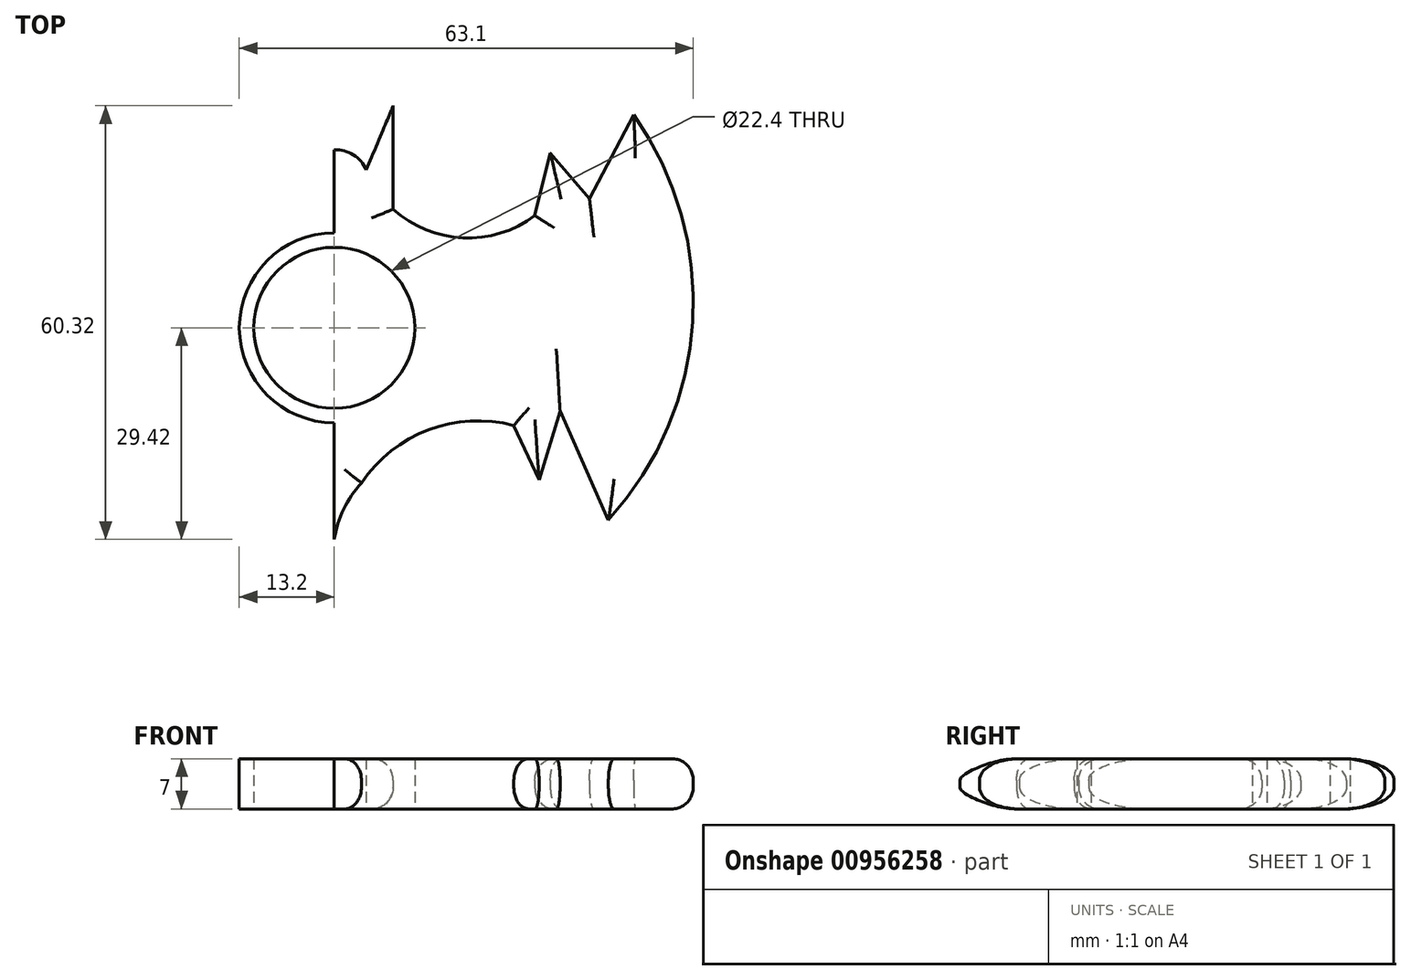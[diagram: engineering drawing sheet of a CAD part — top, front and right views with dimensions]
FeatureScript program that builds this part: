
annotation { "Feature Type Name" : "Feature", "Feature Type Description" : "" }
export const myFeature = defineFeature(function(context is Context, id is Id, definition is map)
    precondition{}
    {
        {
            var Q0;
            Q0=qCreatedBy(makeId("Top.planeOp"),FACE);
            var sketch = newSketch(context, id + "F0", { "sketchPlane" : qUnion([Q0])});
            skCircle(sketch, "E0", {"center": v(0, 0) * mm, "radius": 11.2 * mm});
            skCircle(sketch, "E1", {"center": v(0, 0) * mm, "radius": 13.2 * mm});
            skArc(sketch, "E2", {"start": v(-38.1, 26.72) * mm, "mid": v(-49.82, -0.84) * mm, "end": v(-41.61, -29.64) * mm});
            skArc(sketch, "E3.1.0", {"start": v(38.1, -26.72) * mm, "mid": v(49.82, 0.84) * mm, "end": v(41.61, 29.64) * mm});
            skLineSegment(sketch, "E4", {"start": v(-41.61, -29.64) * mm, "end": v(-35.48, -17.96) * mm});
            skLineSegment(sketch, "E5", {"start": v(-35.48, -17.96) * mm, "end": v(-35.48, -24.97) * mm});
            skArc(sketch, "E6", {"start": v(-4.53, -22.63) * mm, "mid": v(-14.98, -15.03) * mm, "end": v(-27.89, -15.62) * mm});
            skLineSegment(sketch, "E7.1.0", {"start": v(41.61, 29.64) * mm, "end": v(35.48, 17.96) * mm});
            skLineSegment(sketch, "E7.1.1", {"start": v(35.48, 17.96) * mm, "end": v(30.03, 24.29) * mm});
            skLineSegment(sketch, "E7.1.2", {"start": v(30.03, 24.29) * mm, "end": v(27.89, 15.62) * mm});
            skLineSegment(sketch, "E8", {"start": v(38.1, -26.72) * mm, "end": v(31.4, -11.53) * mm});
            skLineSegment(sketch, "E9", {"start": v(31.4, -11.53) * mm, "end": v(28.47, -21.17) * mm});
            skLineSegment(sketch, "E10", {"start": v(28.47, -21.17) * mm, "end": v(24.97, -13.58) * mm});
            skArc(sketch, "E11.1.0", {"start": v(-24.97, 13.58) * mm, "mid": v(-15.85, 12.08) * mm, "end": v(-7.74, 16.5) * mm});
            skLineSegment(sketch, "E11.1.2", {"start": v(-28.47, 21.17) * mm, "end": v(-24.97, 13.58) * mm});
            skLineSegment(sketch, "E11.1.4", {"start": v(-31.4, 11.53) * mm, "end": v(-28.47, 21.17) * mm});
            skLineSegment(sketch, "E11.1.5", {"start": v(-38.1, 26.72) * mm, "end": v(-31.4, 11.53) * mm});
            skArc(sketch, "E12", {"start": v(0, -34.06) * mm, "mid": v(-0.76, -27.75) * mm, "end": v(-4.53, -22.63) * mm});
            skArc(sketch, "E13.1.0", {"start": v(8.2, 16.53) * mm, "mid": v(17.88, 12.52) * mm, "end": v(27.89, 15.62) * mm});
            skLineSegment(sketch, "E14", {"start": v(-7.74, 16.5) * mm, "end": v(-7.74, 29.75) * mm});
            skLineSegment(sketch, "E15", {"start": v(-7.74, 29.75) * mm, "end": v(-4.12, 21.97) * mm});
            skLineSegment(sketch, "E16", {"start": v(8.2, 16.53) * mm, "end": v(8.2, 30.9) * mm});
            skLineSegment(sketch, "E17", {"start": v(8.2, 30.9) * mm, "end": v(4.45, 21.97) * mm});
            skArc(sketch, "E18", {"start": v(4.45, 21.97) * mm, "mid": v(0.16, 24.78) * mm, "end": v(-4.12, 21.97) * mm});
            skArc(sketch, "E19", {"start": v(24.97, -13.58) * mm, "mid": v(13.1, -14.2) * mm, "end": v(3.78, -21.57) * mm});
            skArc(sketch, "E20", {"start": v(3.78, -21.57) * mm, "mid": v(0.47, -27.38) * mm, "end": v(0, -34.06) * mm});
            skLineSegment(sketch, "E21.1.0", {"start": v(-35.48, -17.96) * mm, "end": v(-30.03, -24.29) * mm});
            skLineSegment(sketch, "E21.1.1", {"start": v(-30.03, -24.29) * mm, "end": v(-27.89, -15.62) * mm});
            skLineSegment(sketch, "E22", {"start": v(0, 24.77) * mm, "end": v(0, -34.06) * mm});
            skSolve(sketch);
        }
        {
            var Q0;
            Q0=makeQuery(id+"F0.imprint","IMPRINT",FACE,{"disambiguationData":[TD([[makeQuery(id+"F0.imprint","IMPRINT",EDGE,{"derivedFrom":sQuery(id+"F0.wireOp",EDGE,"E0")}),-1.0]])]});
            var Q1;
            Q1=makeQuery(id+"F0.imprint","IMPRINT",FACE,{"disambiguationData":[TD([[makeQuery(id+"F0.imprint","IMPRINT",EDGE,{"derivedFrom":sQuery(id+"F0.wireOp",EDGE,"E1")}),-1.0]])]});
            extrude(context, id + "F1", {"entities" : qUnion([Q0, Q1]), "depth" : 7 * mm, "offsetDistance" : 25 * mm});
        }
        {
            var Q0;
            Q0=makeQuery(id+"F1.opExtrude","CAP_EDGE",EDGE,{"disambiguationData":[OSD([sQuery(id+"F0.wireOp",EDGE,"E20")])],"isStart":false});
            var Q1;
            Q1=makeQuery(id+"F1.opExtrude","CAP_EDGE",EDGE,{"disambiguationData":[OSD([sQuery(id+"F0.wireOp",EDGE,"E19")])],"isStart":false});
            var Q2;
            Q2=makeQuery(id+"F1.opExtrude","CAP_EDGE",EDGE,{"disambiguationData":[OSD([sQuery(id+"F0.wireOp",EDGE,"E9")])],"isStart":false});
            var Q3;
            Q3=makeQuery(id+"F1.opExtrude","CAP_EDGE",EDGE,{"disambiguationData":[OSD([sQuery(id+"F0.wireOp",EDGE,"E3.1.0")])],"isStart":false});
            var Q4;
            Q4=makeQuery(id+"F1.opExtrude","CAP_EDGE",EDGE,{"disambiguationData":[OSD([sQuery(id+"F0.wireOp",EDGE,"E8")])],"isStart":false});
            var Q5;
            Q5=makeQuery(id+"F1.opExtrude","CAP_EDGE",EDGE,{"disambiguationData":[OSD([sQuery(id+"F0.wireOp",EDGE,"E7.1.0")])],"isStart":false});
            var Q6;
            Q6=makeQuery(id+"F1.opExtrude","CAP_EDGE",EDGE,{"disambiguationData":[OSD([sQuery(id+"F0.wireOp",EDGE,"E7.1.1")])],"isStart":false});
            var Q7;
            Q7=makeQuery(id+"F1.opExtrude","CAP_EDGE",EDGE,{"disambiguationData":[OSD([sQuery(id+"F0.wireOp",EDGE,"E7.1.2")])],"isStart":false});
            var Q8;
            Q8=makeQuery(id+"F1.opExtrude","CAP_EDGE",EDGE,{"disambiguationData":[OSD([sQuery(id+"F0.wireOp",EDGE,"E13.1.0")])],"isStart":false});
            var Q9;
            Q9=makeQuery(id+"F1.opExtrude","CAP_EDGE",EDGE,{"disambiguationData":[OSD([sQuery(id+"F0.wireOp",EDGE,"E16")])],"isStart":false});
            var Q10;
            Q10=makeQuery(id+"F1.opExtrude","CAP_EDGE",EDGE,{"disambiguationData":[OSD([sQuery(id+"F0.wireOp",EDGE,"E14")])],"isStart":false});
            var Q11;
            Q11=makeQuery(id+"F1.opExtrude","CAP_EDGE",EDGE,{"disambiguationData":[OSD([sQuery(id+"F0.wireOp",EDGE,"E11.1.0")])],"isStart":false});
            var Q12;
            Q12=makeQuery(id+"F1.opExtrude","CAP_EDGE",EDGE,{"disambiguationData":[OSD([sQuery(id+"F0.wireOp",EDGE,"E11.1.2")])],"isStart":false});
            var Q13;
            Q13=makeQuery(id+"F1.opExtrude","CAP_EDGE",EDGE,{"disambiguationData":[OSD([sQuery(id+"F0.wireOp",EDGE,"E11.1.5")])],"isStart":false});
            var Q14;
            Q14=makeQuery(id+"F1.opExtrude","CAP_EDGE",EDGE,{"disambiguationData":[OSD([sQuery(id+"F0.wireOp",EDGE,"E11.1.4")])],"isStart":false});
            var Q15;
            Q15=makeQuery(id+"F1.opExtrude","CAP_EDGE",EDGE,{"disambiguationData":[OSD([sQuery(id+"F0.wireOp",EDGE,"E2")])],"isStart":false});
            var Q16;
            Q16=makeQuery(id+"F1.opExtrude","CAP_EDGE",EDGE,{"disambiguationData":[OSD([sQuery(id+"F0.wireOp",EDGE,"E4")])],"isStart":false});
            var Q17;
            Q17=makeQuery(id+"F1.opExtrude","CAP_EDGE",EDGE,{"disambiguationData":[OSD([sQuery(id+"F0.wireOp",EDGE,"wEF84jsq-XExs-cQrN-D3yr-Ib7uIkRzdJAm")])],"isStart":false});
            var Q18;
            Q18=makeQuery(id+"F1.opExtrude","CAP_EDGE",EDGE,{"disambiguationData":[OSD([sQuery(id+"F0.wireOp",EDGE,"E12")])],"isStart":false});
            var Q19;
            Q19=makeQuery(id+"F1.opExtrude","CAP_EDGE",EDGE,{"disambiguationData":[OSD([sQuery(id+"F0.wireOp",EDGE,"E5")])],"isStart":false});
            var Q20;
            Q20=makeQuery(id+"F1.opExtrude","CAP_EDGE",EDGE,{"disambiguationData":[OSD([sQuery(id+"F0.wireOp",EDGE,"E10")])],"isStart":false});
            var Q21;
            Q21=makeQuery(id+"F1.opExtrude","CAP_EDGE",EDGE,{"disambiguationData":[OSD([sQuery(id+"F0.wireOp",EDGE,"E21.1.1")])],"isStart":false});
            var Q22;
            Q22=makeQuery(id+"F1.opExtrude","CAP_EDGE",EDGE,{"disambiguationData":[OSD([sQuery(id+"F0.wireOp",EDGE,"E6")])],"isStart":false});
            var Q23;
            Q23=makeQuery(id+"F1.opExtrude","CAP_EDGE",EDGE,{"disambiguationData":[OSD([sQuery(id+"F0.wireOp",EDGE,"E21.1.0")])],"isStart":false});
            var Q24;
            Q24=makeQuery(id+"F1.opExtrude","CAP_EDGE",EDGE,{"disambiguationData":[OSD([sQuery(id+"F0.wireOp",EDGE,"E3.1.0")])],"isStart":true});
            var Q25;
            Q25=makeQuery(id+"F1.opExtrude","CAP_EDGE",EDGE,{"disambiguationData":[OSD([sQuery(id+"F0.wireOp",EDGE,"E8")])],"isStart":true});
            var Q26;
            Q26=makeQuery(id+"F1.opExtrude","CAP_EDGE",EDGE,{"disambiguationData":[OSD([sQuery(id+"F0.wireOp",EDGE,"E9")])],"isStart":true});
            var Q27;
            Q27=makeQuery(id+"F1.opExtrude","CAP_EDGE",EDGE,{"disambiguationData":[OSD([sQuery(id+"F0.wireOp",EDGE,"E10")])],"isStart":true});
            var Q28;
            Q28=makeQuery(id+"F1.opExtrude","CAP_EDGE",EDGE,{"disambiguationData":[OSD([sQuery(id+"F0.wireOp",EDGE,"E19")])],"isStart":true});
            var Q29;
            Q29=makeQuery(id+"F1.opExtrude","CAP_EDGE",EDGE,{"disambiguationData":[OSD([sQuery(id+"F0.wireOp",EDGE,"E6")])],"isStart":true});
            var Q30;
            Q30=makeQuery(id+"F1.opExtrude","CAP_EDGE",EDGE,{"disambiguationData":[OSD([sQuery(id+"F0.wireOp",EDGE,"E12")])],"isStart":true});
            var Q31;
            Q31=makeQuery(id+"F1.opExtrude","CAP_EDGE",EDGE,{"disambiguationData":[OSD([sQuery(id+"F0.wireOp",EDGE,"E20")])],"isStart":true});
            var Q32;
            Q32=makeQuery(id+"F1.opExtrude","CAP_EDGE",EDGE,{"disambiguationData":[OSD([sQuery(id+"F0.wireOp",EDGE,"E21.1.1")])],"isStart":true});
            var Q33;
            Q33=makeQuery(id+"F1.opExtrude","CAP_EDGE",EDGE,{"disambiguationData":[OSD([sQuery(id+"F0.wireOp",EDGE,"E21.1.0")])],"isStart":true});
            var Q34;
            Q34=makeQuery(id+"F1.opExtrude","CAP_EDGE",EDGE,{"disambiguationData":[OSD([sQuery(id+"F0.wireOp",EDGE,"E4")])],"isStart":true});
            var Q35;
            Q35=makeQuery(id+"F1.opExtrude","CAP_EDGE",EDGE,{"disambiguationData":[OSD([sQuery(id+"F0.wireOp",EDGE,"E2")])],"isStart":true});
            var Q36;
            Q36=makeQuery(id+"F1.opExtrude","CAP_EDGE",EDGE,{"disambiguationData":[OSD([sQuery(id+"F0.wireOp",EDGE,"E11.1.5")])],"isStart":true});
            var Q37;
            Q37=makeQuery(id+"F1.opExtrude","CAP_EDGE",EDGE,{"disambiguationData":[OSD([sQuery(id+"F0.wireOp",EDGE,"E11.1.4")])],"isStart":true});
            var Q38;
            Q38=makeQuery(id+"F1.opExtrude","CAP_EDGE",EDGE,{"disambiguationData":[OSD([sQuery(id+"F0.wireOp",EDGE,"E14")])],"isStart":true});
            var Q39;
            Q39=makeQuery(id+"F1.opExtrude","CAP_EDGE",EDGE,{"disambiguationData":[OSD([sQuery(id+"F0.wireOp",EDGE,"E16")])],"isStart":true});
            var Q40;
            Q40=makeQuery(id+"F1.opExtrude","CAP_EDGE",EDGE,{"disambiguationData":[OSD([sQuery(id+"F0.wireOp",EDGE,"E13.1.0")])],"isStart":true});
            var Q41;
            Q41=makeQuery(id+"F1.opExtrude","CAP_EDGE",EDGE,{"disambiguationData":[OSD([sQuery(id+"F0.wireOp",EDGE,"E7.1.2")])],"isStart":true});
            var Q42;
            Q42=makeQuery(id+"F1.opExtrude","CAP_EDGE",EDGE,{"disambiguationData":[OSD([sQuery(id+"F0.wireOp",EDGE,"E7.1.1")])],"isStart":true});
            var Q43;
            Q43=makeQuery(id+"F1.opExtrude","CAP_EDGE",EDGE,{"disambiguationData":[OSD([sQuery(id+"F0.wireOp",EDGE,"E7.1.0")])],"isStart":true});
            var Q44;
            Q44=makeQuery(id+"F1.opExtrude","CAP_EDGE",EDGE,{"disambiguationData":[OSD([sQuery(id+"F0.wireOp",EDGE,"E11.1.0")])],"isStart":true});
            var Q45;
            Q45=makeQuery(id+"F1.opExtrude","CAP_EDGE",EDGE,{"disambiguationData":[OSD([sQuery(id+"F0.wireOp",EDGE,"E11.1.2")])],"isStart":true});
            fillet(context, id + "F2", {"entities" : qUnion([Q0, Q1, Q2, Q3, Q4, Q5, Q6, Q7, Q8, Q9, Q10, Q11, Q12, Q13, Q14, Q15, Q16, Q17, Q18, Q19, Q20, Q21, Q22, Q23, Q24, Q25, Q26, Q27, Q28, Q29, Q30, Q31, Q32, Q33, Q34, Q35, Q36, Q37, Q38, Q39, Q40, Q41, Q42, Q43, Q44, Q45]), "radius" : 3 * mm, "tangentPropagation" : true, "allowEdgeOverflow" : false});
        }
    });
